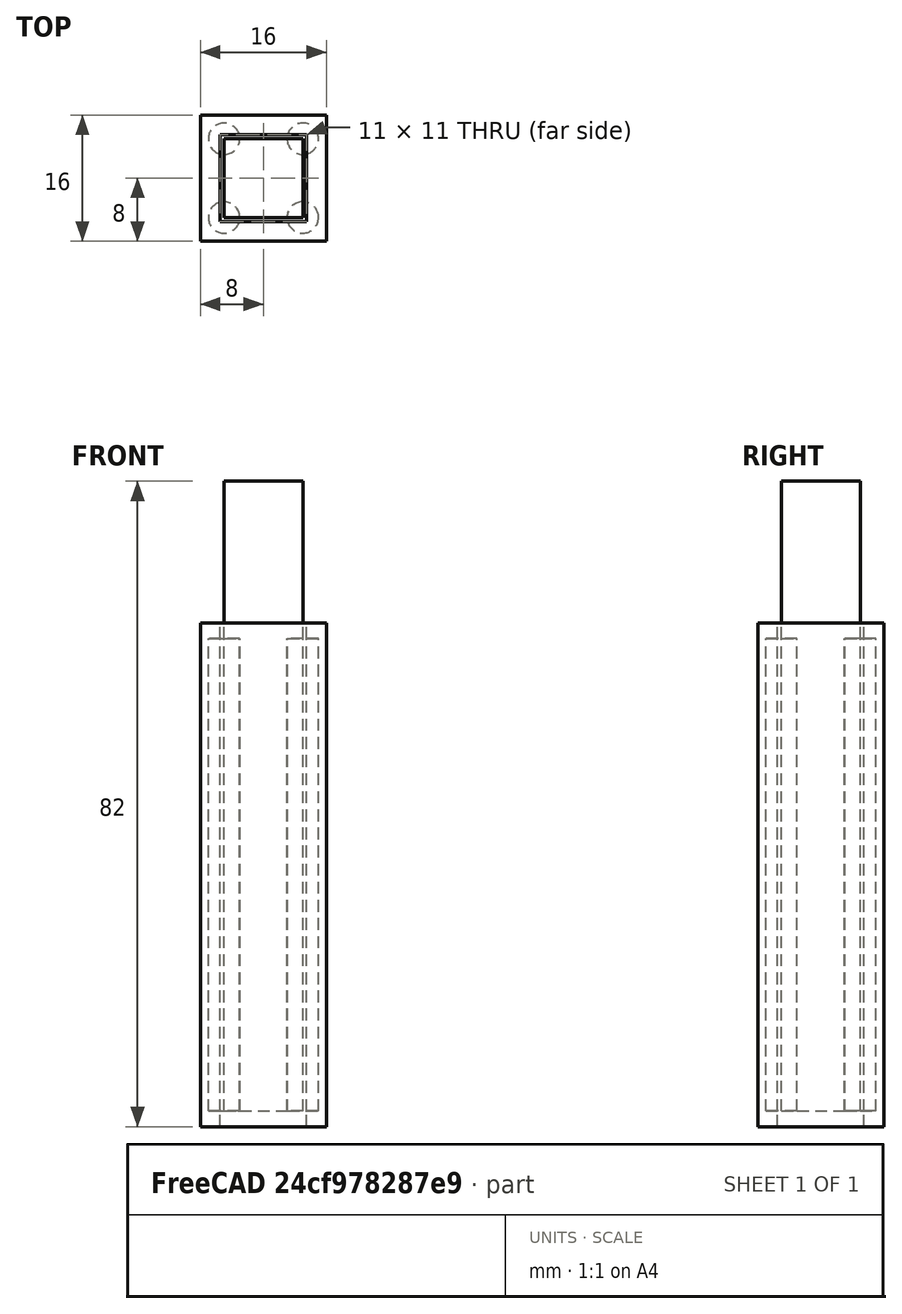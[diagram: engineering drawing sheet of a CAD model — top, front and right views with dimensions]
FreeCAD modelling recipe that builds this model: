
FCSTD DOCUMENT  (FreeCAD 0.14R3692 (Git))
Label: actuator1
License: CC-BY 3.0
LicenseURL: http://creativecommons.org/licenses/by/3.0/
objects: Part::Cut×9, Part::Cylinder×8, Part::Box×3
note: 20 computed .brp shape members not serialized (recipe doc carries the construction recipe); baked Part::Feature solids carry a one-line shape summary decoded from their .brp

FEATURE [Part::Cylinder] Cylinder
  Angle = 360
  Height = 60
  Radius = 2
FEATURE [Part::Cylinder] Cylinder001
  Angle = 360
  Height = 60
  Placement = pos=(10,0,0) rot=(0,0,1;0rad)
  Radius = 2
FEATURE [Part::Cylinder] Cylinder002
  Angle = 360
  Height = 60
  Placement = pos=(10,10,0) rot=(0,0,1;0rad)
  Radius = 2
FEATURE [Part::Cylinder] Cylinder003
  Angle = 360
  Height = 60
  Placement = pos=(0,10,0) rot=(0,0,1;0rad)
  Radius = 2
FEATURE [Part::Box] Box  label="Cube"
  Height = 80
  Length = 10
  Width = 10
FEATURE [Part::Cylinder] Cylinder004
  Angle = 360
  Height = 60
  Radius = 2
FEATURE [Part::Cylinder] Cylinder005
  Angle = 360
  Height = 60
  Placement = pos=(0,10,0) rot=(0,0,1;0rad)
  Radius = 2
FEATURE [Part::Cylinder] Cylinder006
  Angle = 360
  Height = 60
  Placement = pos=(10,10,0) rot=(0,0,1;0rad)
  Radius = 2
FEATURE [Part::Cylinder] Cylinder007
  Angle = 360
  Height = 60
  Placement = pos=(10,0,0) rot=(0,0,1;0rad)
  Radius = 2
FEATURE [Part::Cut] Cut
  Base = -> Box
  Tool = -> Cylinder004
FEATURE [Part::Cut] Cut001
  Base = -> Cut
  Tool = -> Cylinder007
FEATURE [Part::Cut] Cut002
  Base = -> Cut001
  Tool = -> Cylinder006
FEATURE [Part::Cut] Cut003
  Base = -> Cut002
  Tool = -> Cylinder005
FEATURE [Part::Box] Box001  label="Cube001"
  Height = 64
  Length = 16
  Placement = pos=(-3,-3,-2) rot=(0,0,1;0rad)
  Width = 16
FEATURE [Part::Box] Box002  label="Cube002"
  Height = 80
  Length = 11
  Placement = pos=(-0.5,-0.5,-5) rot=(0,0,1;0rad)
  Width = 11
FEATURE [Part::Cut] Cut004
  Base = -> Box001
  Tool = -> Box002
FEATURE [Part::Cut] Cut005
  Base = -> Cut004
  Tool = -> Cylinder003
FEATURE [Part::Cut] Cut006
  Base = -> Cut005
  Tool = -> Cylinder001
FEATURE [Part::Cut] Cut007
  Base = -> Cut006
  Tool = -> Cylinder002
FEATURE [Part::Cut] Cut008
  Base = -> Cut007
  Tool = -> Cylinder
